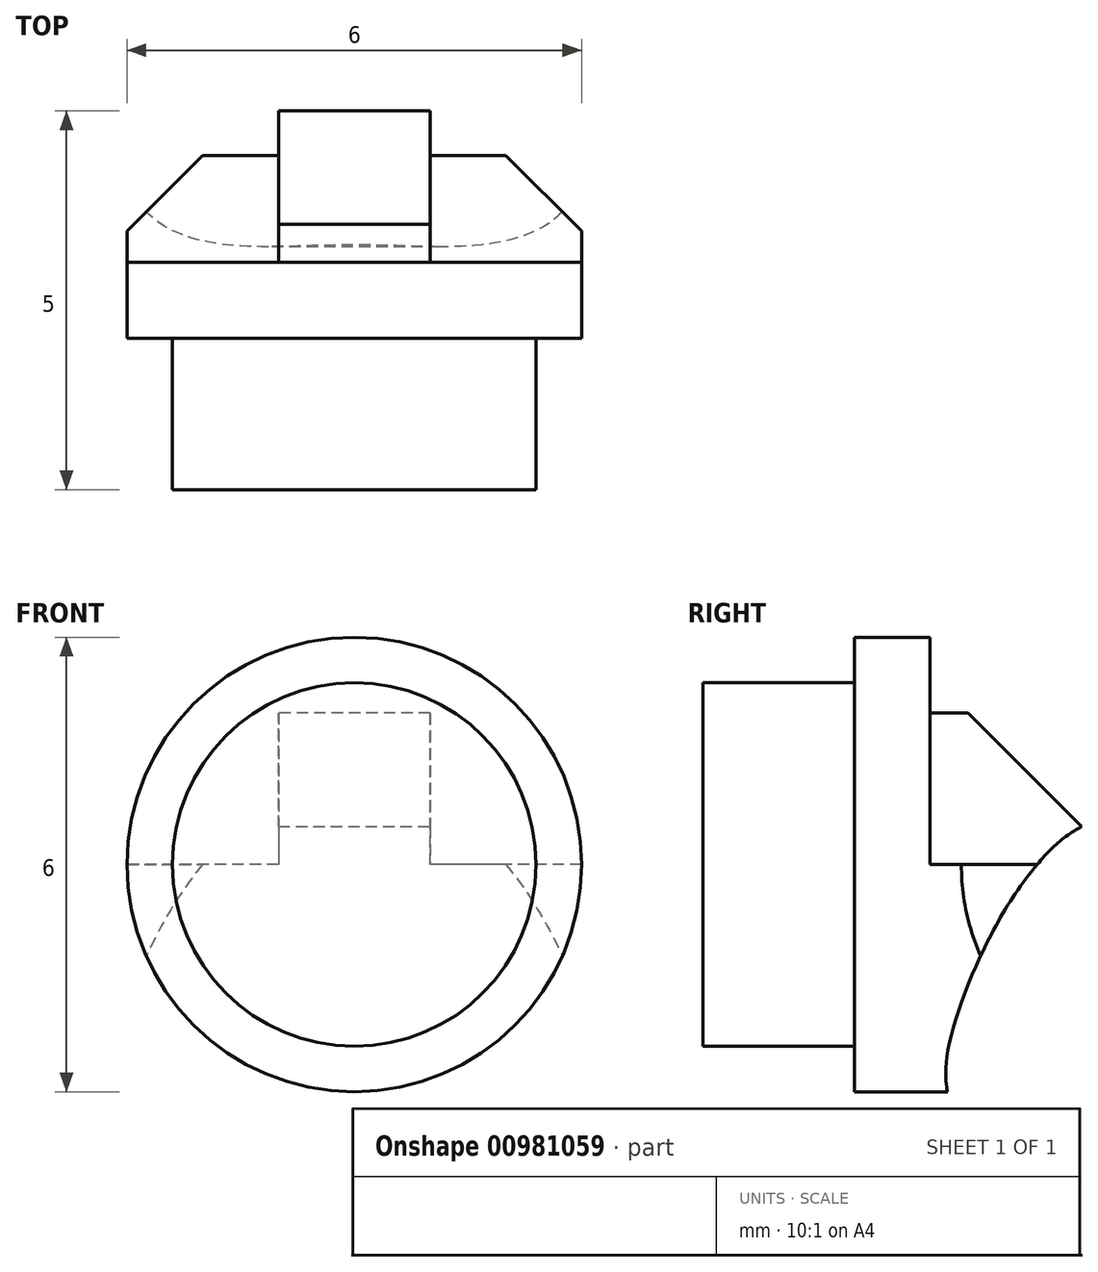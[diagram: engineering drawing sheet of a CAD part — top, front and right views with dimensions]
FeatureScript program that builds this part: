
annotation { "Feature Type Name" : "Feature", "Feature Type Description" : "" }
export const myFeature = defineFeature(function(context is Context, id is Id, definition is map)
    precondition{}
    {
        {
            var Q0;
            Q0=qCreatedBy(makeId("Front.planeOp"),FACE);
            var sketch = newSketch(context, id + "F0", { "sketchPlane" : qUnion([Q0])});
            skCircle(sketch, "E0", {"center": v(0, 0) * mm, "radius": 3 * mm});
            skSolve(sketch);
        }
        {
            var Q0;
            Q0=makeQuery(id+"F0.imprint","IMPRINT",FACE,{"disambiguationData":[TD([[makeQuery(id+"F0.imprint","IMPRINT",EDGE,{"derivedFrom":sQuery(id+"F0.wireOp",EDGE,"E0")}),1.0]])]});
            extrude(context, id + "F1", {"entities" : qUnion([Q0]), "depth" : 1 * mm, "offsetDistance" : 25 * mm});
        }
        {
            var Q0;
            Q0=makeQuery(id+"F1.opExtrude","CAP_FACE",FACE,{"disambiguationData":[OSD([sQuery(id+"F0.wireOp",EDGE,"E0")])],"isStart":false});
            var sketch = newSketch(context, id + "F2", { "sketchPlane" : qUnion([Q0])});
            skCircle(sketch, "E1", {"center": v(0, 0) * mm, "radius": 2.4 * mm});
            skCircle(sketch, "E2", {"center": v(0, 0) * mm, "radius": 1.4 * mm});
            skSolve(sketch);
        }
        {
            var Q0;
            Q0=makeQuery(id+"F2.imprint","IMPRINT",FACE,{"disambiguationData":[TD([[makeQuery(id+"F2.imprint","IMPRINT",EDGE,{"derivedFrom":sQuery(id+"F2.wireOp",EDGE,"E1")}),1.0]])]});
            var Q1;
            Q1=makeQuery(id+"F2.imprint","IMPRINT",FACE,{"disambiguationData":[TD([[makeQuery(id+"F2.imprint","IMPRINT",EDGE,{"derivedFrom":sQuery(id+"F2.wireOp",EDGE,"E2")}),1.0]])]});
            extrude(context, id + "F3", {"entities" : qUnion([Q0, Q1]), "operationType" : NewBodyOperationType.ADD, "depth" : 2 * mm, "offsetDistance" : 25 * mm});
        }
        {
            var Q0;
            Q0=makeQuery(id+"F1.opExtrude","CAP_FACE",FACE,{"disambiguationData":[OSD([sQuery(id+"F0.wireOp",EDGE,"E0")])],"isStart":true});
            var sketch = newSketch(context, id + "F4", { "sketchPlane" : qUnion([Q0])});
            skArc(sketch, "E3", {"start": v(-3, 0) * mm, "mid": v(0, -3) * mm, "end": v(3, 0) * mm});
            skLineSegment(sketch, "E4", {"start": v(-3, 0) * mm, "end": v(3, 0) * mm});
            skLineSegment(sketch, "E5", {"start": v(-1, 0) * mm, "end": v(-1, 2) * mm});
            skLineSegment(sketch, "E6", {"start": v(-1, 2) * mm, "end": v(1, 2) * mm});
            skLineSegment(sketch, "E7", {"start": v(1, 2) * mm, "end": v(1, 0) * mm});
            skSolve(sketch);
        }
        {
            var Q0;
            {var subQ0=sQuery(id+"F4.wireOp",EDGE,"E5");Q0=makeQuery(id+"F4.imprint","IMPRINT",FACE,{"disambiguationData":[TD([[makeQuery(id+"F4.imprint","IMPRINT",EDGE,{"derivedFrom":subQ0}),-1.0]])]});}
            var Q1;
            {var subQ0=sQuery(id+"F4.wireOp",EDGE,"E3");Q1=makeQuery(id+"F4.imprint","IMPRINT",FACE,{"disambiguationData":[TD([[makeQuery(id+"F4.imprint","IMPRINT",EDGE,{"derivedFrom":subQ0}),-1.0]])]});}
            extrude(context, id + "F5", {"entities" : qUnion([Q0, Q1]), "operationType" : NewBodyOperationType.ADD, "depth" : 2 * mm, "offsetDistance" : 25 * mm});
        }
        {
            var Q0;
            Q0=makeQuery(id+"F5.opExtrude","CAP_EDGE",EDGE,{"disambiguationData":[OSD([sQuery(id+"F4.wireOp",EDGE,"E6")])],"isStart":false});
            chamfer(context, id + "F6", {"entities" : qUnion([Q0]), "width" : 1.5 * mm, "tangentPropagation" : true});
        }
        {
            var Q0;
            Q0=makeQuery(id+"F5.opExtrude","SWEPT_FACE",FACE,{"disambiguationData":[OSD([sQuery(id+"F4.wireOp",EDGE,"E7")])]});
            var sketch = newSketch(context, id + "F7", { "sketchPlane" : qUnion([Q0])});
            skLineSegment(sketch, "E8", {"start": v(-2, 0.5) * mm, "end": v(-2, -3) * mm});
            skLineSegment(sketch, "E9", {"start": v(-2, -3) * mm, "end": v(-0.23, -3) * mm});
            skFitSpline(sketch, "E10", {"points": [v(-2, 0.5) * mm, v(-0.23, -3) * mm], "startDerivative": vector(3, -1.5) * mm, "endDerivative": vector(-0.7, -1.64) * mm});
            skSolve(sketch);
        }
        {
            var Q0;
            {var subQ0=sQuery(id+"F7.wireOp",EDGE,"E8");var subQ1=sQuery(id+"F4.wireOp",EDGE,"E7");var subQ2=makeQuery(id+"F5.opExtrude","SWEPT_EDGE",EDGE,{"disambiguationData":[OSD([sQuery(id+"F4.wireOp",EDGE,"E4"),subQ1])]});var subQ3=makeQuery(id+"F7.imprint","INTERSECT",VERTEX,{"derivedFrom":[subQ2,subQ0]});Q0=makeQuery(id+"F7.imprint","IMPRINT",FACE,{"disambiguationData":[TD([[makeQuery(id+"F7.imprint","IMPRINT",EDGE,{"disambiguationData":[TD([[subQ3,1.0]])],"derivedFrom":subQ0}),1.0]])]});}
            var Q1;
            {var subQ3=sQuery(id+"F7.wireOp",EDGE,"E9");Q1=makeQuery(id+"F7.imprint","IMPRINT",FACE,{"disambiguationData":[TD([[makeQuery(id+"F7.imprint","IMPRINT",EDGE,{"derivedFrom":subQ3}),1.0]])]});}
            extrude(context, id + "F8", {"entities" : qUnion([Q0, Q1]), "operationType" : NewBodyOperationType.REMOVE, "oppositeDirection" : true, "depth" : 25 * mm, "offsetDistance" : 25 * mm, "hasSecondDirection" : true, "secondDirectionOppositeDirection" : false, "secondDirectionDepth" : 25 * mm});
        }
        {
            var Q0;
            {var subQ0=sQuery(id+"F4.wireOp",EDGE,"E4");Q0=makeQuery(id+"F5.opExtrude","SWEPT_FACE",FACE,{"disambiguationData":[OSD([subQ0]),TDD([makeQuery(id+"F4.imprint","IMPRINT",EDGE,{"disambiguationData":[TD([[makeQuery(id+"F4.imprint","INTERSECT",VERTEX,{"derivedFrom":[subQ0,sQuery(id+"F4.wireOp",EDGE,"E5")]}),1.0]])],"derivedFrom":subQ0})])]});}
            var sketch = newSketch(context, id + "F9", { "sketchPlane" : qUnion([Q0])});
            skLineSegment(sketch, "E11", {"start": v(3, 1.41) * mm, "end": v(3, 0.41) * mm});
            skLineSegment(sketch, "E12", {"start": v(3, 0.41) * mm, "end": v(2, 1.41) * mm});
            skLineSegment(sketch, "E13", {"start": v(2, 1.41) * mm, "end": v(3, 1.41) * mm});
            skSolve(sketch);
        }
        {
            var Q0;
            {var subQ0=sQuery(id+"F4.wireOp",EDGE,"E4");Q0=makeQuery(id+"F5.opExtrude","SWEPT_FACE",FACE,{"disambiguationData":[OSD([subQ0]),TDD([makeQuery(id+"F4.imprint","IMPRINT",EDGE,{"disambiguationData":[TD([[makeQuery(id+"F4.imprint","INTERSECT",VERTEX,{"derivedFrom":[subQ0,sQuery(id+"F4.wireOp",EDGE,"E7")]}),-1.0]])],"derivedFrom":subQ0})])]});}
            var sketch = newSketch(context, id + "F10", { "sketchPlane" : qUnion([Q0])});
            skLineSegment(sketch, "E14", {"start": v(-3, 1.41) * mm, "end": v(-2, 1.41) * mm});
            skLineSegment(sketch, "E15", {"start": v(-3, 1.41) * mm, "end": v(-3, 0.41) * mm});
            skLineSegment(sketch, "E16", {"start": v(-3, 0.41) * mm, "end": v(-2, 1.41) * mm});
            skSolve(sketch);
        }
        {
            var Q0;
            Q0=makeQuery(id+"F10.imprint","IMPRINT",FACE,{"disambiguationData":[TD([[makeQuery(id+"F10.imprint","IMPRINT",EDGE,{"derivedFrom":sQuery(id+"F10.wireOp",EDGE,"E14")}),1.0]])]});
            var Q1;
            Q1=makeQuery(id+"F9.imprint","IMPRINT",FACE,{"disambiguationData":[TD([[makeQuery(id+"F9.imprint","IMPRINT",EDGE,{"derivedFrom":sQuery(id+"F9.wireOp",EDGE,"E11")}),-1.0]])]});
            extrude(context, id + "F11", {"entities" : qUnion([Q0, Q1]), "operationType" : NewBodyOperationType.REMOVE, "oppositeDirection" : true, "depth" : 25 * mm, "offsetDistance" : 25 * mm});
        }
    });
